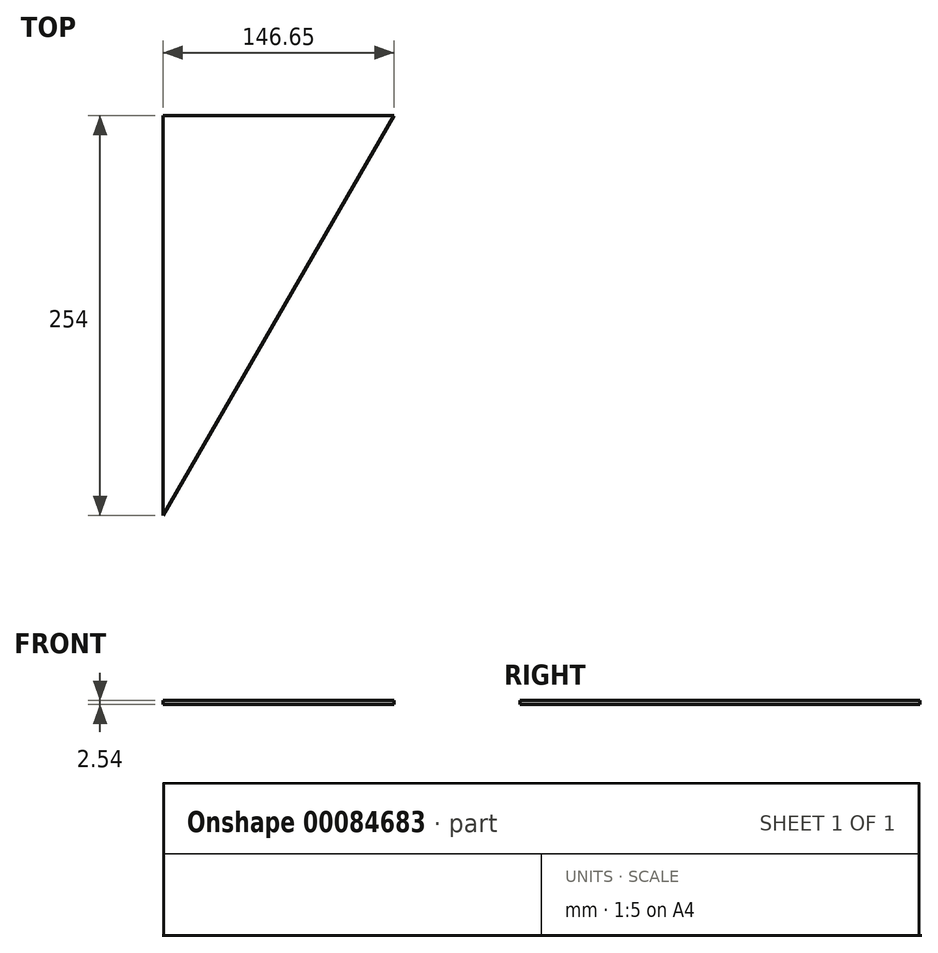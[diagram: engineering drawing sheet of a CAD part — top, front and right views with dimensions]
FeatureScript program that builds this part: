
annotation { "Feature Type Name" : "Feature", "Feature Type Description" : "" }
export const myFeature = defineFeature(function(context is Context, id is Id, definition is map)
    precondition{}
    {
        {
            var Q0;
            Q0=qCreatedBy(makeId("Top.planeOp"),FACE);
            var sketch = newSketch(context, id + "F0", { "sketchPlane" : qUnion([Q0])});
            skCircle(sketch, "E0.cCircle", {"center": v(0, 0) * mm, "radius": 50.8 * mm, "construction": true});
            skLineSegment(sketch, "E0.0", {"start": v(44, -25.4) * mm, "end": v(0, -50.8) * mm});
            skLineSegment(sketch, "E0.1", {"start": v(0, -50.8) * mm, "end": v(-44, -25.4) * mm});
            skLineSegment(sketch, "E0.2", {"start": v(-44, -25.4) * mm, "end": v(-44, 25.4) * mm});
            skLineSegment(sketch, "E0.3", {"start": v(-44, 25.4) * mm, "end": v(0, 50.8) * mm});
            skLineSegment(sketch, "E0.4", {"start": v(0, 50.8) * mm, "end": v(44, 25.4) * mm});
            skLineSegment(sketch, "E0.5", {"start": v(44, 25.4) * mm, "end": v(44, -25.4) * mm});
            skLineSegment(sketch, "E1", {"start": v(-44, 50.8) * mm, "end": v(44, 50.8) * mm});
            skLineSegment(sketch, "E2", {"start": v(44, -50.8) * mm, "end": v(-44, -50.8) * mm});
            skLineSegment(sketch, "E3", {"start": v(-44, 50.8) * mm, "end": v(-33, 31.75) * mm});
            skLineSegment(sketch, "E4", {"start": v(41.25, 74.62) * mm, "end": v(-138.37, -29.09) * mm});
            skLineSegment(sketch, "E5", {"start": v(-119.84, 242.1) * mm, "end": v(-119.84, 220.1) * mm, "construction": true});
            skLineSegment(sketch, "E6", {"start": v(-132.54, 220.1) * mm, "end": v(-81.74, 220.1) * mm});
            skLineSegment(sketch, "E7", {"start": v(-81.74, 220.1) * mm, "end": v(-132.54, 249.42) * mm});
            skLineSegment(sketch, "E8", {"start": v(-132.54, 220.1) * mm, "end": v(-157.94, 176.1) * mm});
            skLineSegment(sketch, "E9", {"start": v(-81.74, 220.1) * mm, "end": v(-157.94, 176.1) * mm, "construction": true});
            skLineSegment(sketch, "E10", {"start": v(-44, 25.4) * mm, "end": v(44, 25.4) * mm});
            skLineSegment(sketch, "E11", {"start": v(-132.54, 220.1) * mm, "end": v(-119.84, 242.1) * mm});
            skLineSegment(sketch, "E12", {"start": v(-326.23, 220.1) * mm, "end": v(147.87, 220.1) * mm, "construction": true});
            skLineSegment(sketch, "E13", {"start": v(-282.85, 220.1) * mm, "end": v(-282.85, -40.25) * mm});
            skLineSegment(sketch, "E14", {"start": v(-282.85, 213.75) * mm, "end": v(-136.2, 213.75) * mm});
            skLineSegment(sketch, "E15", {"start": v(-136.2, 213.75) * mm, "end": v(-282.85, -40.25) * mm});
            skLineSegment(sketch, "E16", {"start": v(-157.94, 176.1) * mm, "end": v(-36.36, 176.1) * mm, "construction": true});
            skLineSegment(sketch, "E17.MirrorCS", {"start": v(-132.54, 132.1) * mm, "end": v(-81.74, 132.1) * mm});
            skLineSegment(sketch, "E18.MirrorCS", {"start": v(-132.54, 132.1) * mm, "end": v(-157.94, 176.1) * mm});
            skLineSegment(sketch, "E19", {"start": v(-107.14, 132.1) * mm, "end": v(-107.14, 176.1) * mm, "construction": true});
            skLineSegment(sketch, "E20.MirrorCS", {"start": v(-81.74, 132.1) * mm, "end": v(-56.34, 176.1) * mm});
            skLineSegment(sketch, "E21.MirrorCS", {"start": v(-81.74, 220.1) * mm, "end": v(-56.34, 176.1) * mm});
            skSolve(sketch);
        }
        {
            var Q0;
            {var subQ3=sQuery(id+"F0.wireOp",EDGE,"E14");Q0=makeQuery(id+"F0.imprint","IMPRINT",FACE,{"disambiguationData":[TD([[makeQuery(id+"F0.imprint","IMPRINT",EDGE,{"derivedFrom":subQ3}),-1.0]])]});}
            extrude(context, id + "F1", {"entities" : qUnion([Q0]), "depth" : 2.54 * mm});
        }
    });
